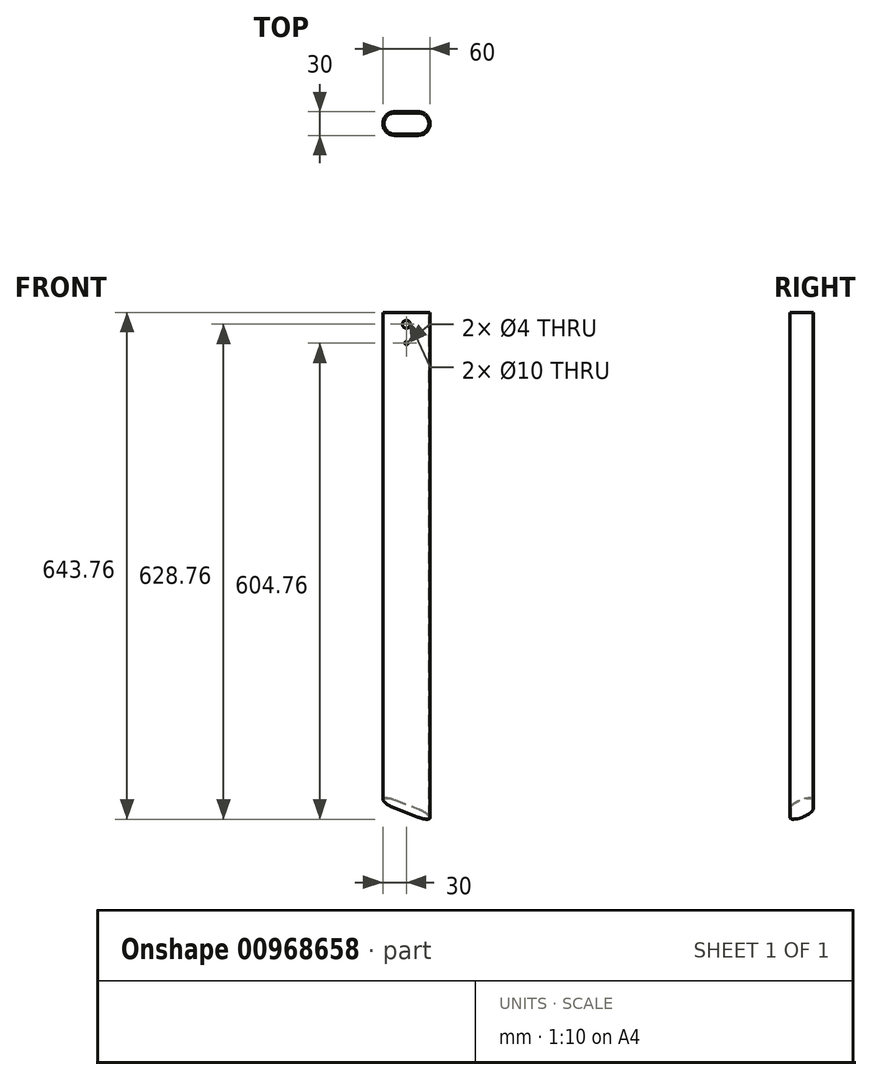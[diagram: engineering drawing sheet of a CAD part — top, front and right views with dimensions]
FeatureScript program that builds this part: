
annotation { "Feature Type Name" : "Feature", "Feature Type Description" : "" }
export const myFeature = defineFeature(function(context is Context, id is Id, definition is map)
    precondition{}
    {
        {
            var Q0;
            Q0=qCreatedBy(makeId("Top.planeOp"),FACE);
            var sketch = newSketch(context, id + "F0", { "sketchPlane" : qUnion([Q0])});
            skLineSegment(sketch, "E0.bottom", {"start": v(-15, 15) * mm, "end": v(15, 15) * mm});
            skLineSegment(sketch, "E0.top", {"start": v(-15, -15) * mm, "end": v(15, -15) * mm});
            skLineSegment(sketch, "E0.left", {"start": v(-30, 0) * mm, "end": v(-30, 0) * mm});
            skLineSegment(sketch, "E0.right", {"start": v(30, 0) * mm, "end": v(30, 0) * mm});
            skPoint(sketch, "E0.middle", {"position": v(0, 0) * mm});
            skPoint(sketch, "E1.visualSharp", {"position": v(-30, 15) * mm});
            skArc(sketch, "E1.filletArc", {"start": v(-15, 15) * mm, "mid": v(-25.6, 10.6) * mm, "end": v(-30, 0) * mm});
            skPoint(sketch, "E2.visualSharp", {"position": v(-30, -15) * mm});
            skArc(sketch, "E2.filletArc", {"start": v(-30, 0) * mm, "mid": v(-25.6, -10.6) * mm, "end": v(-15, -15) * mm});
            skPoint(sketch, "E3.visualSharp", {"position": v(30, -15) * mm});
            skArc(sketch, "E3.filletArc", {"start": v(15, -15) * mm, "mid": v(25.6, -10.6) * mm, "end": v(30, 0) * mm});
            skPoint(sketch, "E4.visualSharp", {"position": v(30, 15) * mm});
            skArc(sketch, "E4.filletArc", {"start": v(30, 0) * mm, "mid": v(25.6, 10.6) * mm, "end": v(15, 15) * mm});
            skLineSegment(sketch, "E5.bottom", {"start": v(-15, 13.5) * mm, "end": v(15, 13.5) * mm});
            skLineSegment(sketch, "E5.top", {"start": v(-15, -13.5) * mm, "end": v(15, -13.5) * mm});
            skLineSegment(sketch, "E5.left", {"start": v(-28.5, 0) * mm, "end": v(-28.5, 0) * mm});
            skLineSegment(sketch, "E5.right", {"start": v(28.5, 0) * mm, "end": v(28.5, 0) * mm});
            skPoint(sketch, "E6.visualSharp", {"position": v(-28.5, 13.5) * mm});
            skArc(sketch, "E6.filletArc", {"start": v(-15, 13.5) * mm, "mid": v(-24.55, 9.55) * mm, "end": v(-28.5, 0) * mm});
            skPoint(sketch, "E7.visualSharp", {"position": v(-28.5, -13.5) * mm});
            skArc(sketch, "E7.filletArc", {"start": v(-28.5, 0) * mm, "mid": v(-24.55, -9.55) * mm, "end": v(-15, -13.5) * mm});
            skPoint(sketch, "E8.visualSharp", {"position": v(28.5, -13.5) * mm});
            skArc(sketch, "E8.filletArc", {"start": v(15, -13.5) * mm, "mid": v(24.55, -9.55) * mm, "end": v(28.5, 0) * mm});
            skPoint(sketch, "E9.visualSharp", {"position": v(28.5, 13.5) * mm});
            skArc(sketch, "E9.filletArc", {"start": v(28.5, 0) * mm, "mid": v(24.55, 9.55) * mm, "end": v(15, 13.5) * mm});
            skSolve(sketch);
        }
        {
            var Q0;
            Q0=qSketchRegion(id+"F0",true);
            extrude(context, id + "F1", {"entities" : qUnion([Q0]), "oppositeDirection" : true, "depth" : 644 * mm, "offsetDistance" : 25 * mm});
        }
        {
            var Q0;
            Q0=makeQuery(id+"F1.opExtrude","SWEPT_FACE",FACE,{"disambiguationData":[OSD([sQuery(id+"F0.wireOp",EDGE,"E0.bottom")])]});
            var sketch = newSketch(context, id + "F2", { "sketchPlane" : qUnion([Q0])});
            skLineSegment(sketch, "E10.0", {"start": v(15, 0) * mm, "end": v(-15, 0) * mm, "construction": true});
            skLineSegment(sketch, "E11", {"start": v(0, 0) * mm, "end": v(0, -15) * mm, "construction": true});
            skCircle(sketch, "E12", {"center": v(0, -15) * mm, "radius": 5 * mm});
            skLineSegment(sketch, "E13", {"start": v(0, -15) * mm, "end": v(0, -39) * mm, "construction": true});
            skCircle(sketch, "E14", {"center": v(0, -39) * mm, "radius": 2 * mm});
            skSolve(sketch);
        }
        {
            var Q0;
            Q0=makeQuery(id+"F2.imprint","IMPRINT",FACE,{"disambiguationData":[TD([[makeQuery(id+"F2.imprint","IMPRINT",EDGE,{"derivedFrom":sQuery(id+"F2.wireOp",EDGE,"E12")}),1.0]])]});
            var Q1;
            Q1=makeQuery(id+"F2.imprint","IMPRINT",FACE,{"disambiguationData":[TD([[makeQuery(id+"F2.imprint","IMPRINT",EDGE,{"derivedFrom":sQuery(id+"F2.wireOp",EDGE,"E14")}),1.0]])]});
            extrude(context, id + "F3", {"entities" : qUnion([Q0, Q1]), "operationType" : NewBodyOperationType.REMOVE, "oppositeDirection" : true, "depth" : 40 * mm, "offsetDistance" : 25 * mm});
        }
        {
            var Q0;
            Q0=makeQuery(id+"F1.opExtrude","CAP_FACE",FACE,{"disambiguationData":[OSD([sQuery(id+"F0.wireOp",EDGE,"E0.bottom"),sQuery(id+"F0.wireOp",EDGE,"E0.top"),sQuery(id+"F0.wireOp",EDGE,"E1.filletArc"),sQuery(id+"F0.wireOp",EDGE,"E2.filletArc"),sQuery(id+"F0.wireOp",EDGE,"E3.filletArc"),sQuery(id+"F0.wireOp",EDGE,"E4.filletArc"),sQuery(id+"F0.wireOp",EDGE,"E5.bottom"),sQuery(id+"F0.wireOp",EDGE,"E5.top"),sQuery(id+"F0.wireOp",EDGE,"E6.filletArc"),sQuery(id+"F0.wireOp",EDGE,"E7.filletArc"),sQuery(id+"F0.wireOp",EDGE,"E8.filletArc"),sQuery(id+"F0.wireOp",EDGE,"E9.filletArc")])],"isStart":false});
            var sketch = newSketch(context, id + "F4", { "sketchPlane" : qUnion([Q0])});
            skLineSegment(sketch, "E15.bottom", {"start": v(-15, 13.5) * mm, "end": v(15, 13.5) * mm});
            skLineSegment(sketch, "E15.top", {"start": v(-15, -13.5) * mm, "end": v(15, -13.5) * mm});
            skLineSegment(sketch, "E15.left", {"start": v(-15, 13.5) * mm, "end": v(-15, -13.5) * mm});
            skLineSegment(sketch, "E15.right", {"start": v(15, 13.5) * mm, "end": v(15, -13.5) * mm});
            skCircle(sketch, "E16", {"center": v(0, 0) * mm, "radius": 5 * mm});
            skSolve(sketch);
        }
        {
            var Q0;
            Q0=makeQuery(id+"F1.opExtrude","CAP_FACE",FACE,{"disambiguationData":[OSD([sQuery(id+"F0.wireOp",EDGE,"E0.bottom"),sQuery(id+"F0.wireOp",EDGE,"E0.top"),sQuery(id+"F0.wireOp",EDGE,"E1.filletArc"),sQuery(id+"F0.wireOp",EDGE,"E2.filletArc"),sQuery(id+"F0.wireOp",EDGE,"E3.filletArc"),sQuery(id+"F0.wireOp",EDGE,"E4.filletArc"),sQuery(id+"F0.wireOp",EDGE,"E5.bottom"),sQuery(id+"F0.wireOp",EDGE,"E5.top"),sQuery(id+"F0.wireOp",EDGE,"E6.filletArc"),sQuery(id+"F0.wireOp",EDGE,"E7.filletArc"),sQuery(id+"F0.wireOp",EDGE,"E8.filletArc"),sQuery(id+"F0.wireOp",EDGE,"E9.filletArc")])],"isStart":false});
            var Q1;
            Q1=makeQuery(id+"F1.opExtrude","CAP_EDGE",EDGE,{"disambiguationData":[OSD([sQuery(id+"F0.wireOp",EDGE,"E0.top")])],"isStart":false});
            cPlane(context, id + "F5", {"entities" : qUnion([Q0, Q1]), "cplaneType" : CPlaneType.LINE_ANGLE, "offset" : 25 * mm, "angle" : 20 * degree, "width" : 150 * mm, "height" : 150 * mm});
        }
        {
            var Q0;
            Q0=qCreatedBy(id+"F5.planeOp",FACE);
            var sketch = newSketch(context, id + "F6", { "sketchPlane" : qUnion([Q0])});
            skLineSegment(sketch, "E17.bottom", {"start": v(-10.06, -238.6) * mm, "end": v(10.06, -238.6) * mm});
            skLineSegment(sketch, "E17.top", {"start": v(-10.06, -222.21) * mm, "end": v(10.06, -222.21) * mm});
            skLineSegment(sketch, "E17.left", {"start": v(-10.06, -238.6) * mm, "end": v(-10.06, -222.21) * mm});
            skLineSegment(sketch, "E17.right", {"start": v(10.06, -238.6) * mm, "end": v(10.06, -222.21) * mm});
            skPoint(sketch, "E17.middle", {"position": v(0, -230.4) * mm});
            skSolve(sketch);
        }
        {
            var Q0;
            Q0=qCreatedBy(id+"F5.planeOp",FACE);
            var Q1;
            Q1=sQuery(id+"F6.wireOp",EDGE,"E17.left");
            cPlane(context, id + "F7", {"entities" : qUnion([Q0, Q1]), "cplaneType" : CPlaneType.LINE_ANGLE, "offset" : 25 * mm, "angle" : 20 * degree, "width" : 150 * mm, "height" : 150 * mm});
        }
        {
            var Q0;
            Q0=qCreatedBy(id+"F7.planeOp",FACE);
            var sketch = newSketch(context, id + "F8", { "sketchPlane" : qUnion([Q0])});
            skLineSegment(sketch, "E18.bottom", {"start": v(159.08, 261.24) * mm, "end": v(254, 261.24) * mm});
            skLineSegment(sketch, "E18.top", {"start": v(159.08, 177.89) * mm, "end": v(254, 177.89) * mm});
            skLineSegment(sketch, "E18.left", {"start": v(159.08, 261.24) * mm, "end": v(159.08, 177.89) * mm});
            skLineSegment(sketch, "E18.right", {"start": v(254, 261.24) * mm, "end": v(254, 177.89) * mm});
            skPoint(sketch, "E18.middle", {"position": v(206.54, 219.56) * mm});
            skSolve(sketch);
        }
        {
            var Q0;
            Q0=makeQuery(id+"F8.imprint","IMPRINT",FACE,{"disambiguationData":[TD([[makeQuery(id+"F8.imprint","IMPRINT",EDGE,{"derivedFrom":sQuery(id+"F8.wireOp",EDGE,"E18.bottom")}),-1.0]])]});
            extrude(context, id + "F9", {"entities" : qUnion([Q0]), "operationType" : NewBodyOperationType.REMOVE, "oppositeDirection" : true, "depth" : 11 * mm, "offsetDistance" : 25 * mm, "hasSecondDirection" : true, "secondDirectionOppositeDirection" : false, "secondDirectionDepth" : 25 * mm});
        }
    });
